# Revit family: assa_abloy_sw200i_13
name_source: partatom
category: Doors
units: mm (PartAtom-declared; Revit-internal decimal feet)

## family parameters
Always vertical = Yes
Classification Number = 23.30.10.00
Cut with Voids When Loaded = No
Host = Wall
Room Calculation Point = No
Shared = No

## types (1)
- assa_abloy_sw200i_13
    Analytic Construction = <None>
    BIMobject category = Swing Doors
    Bottom Profile Height = Leaf : 0' 4''
    Bottom Profile Option 01 = Leaf : 0' 4''
    Bottom Profile Option 02 = Leaf : 0' 7''
    Bottom Profile Option 03 = Leaf : 0' 10''
    Bottom Profile Option 04 = Leaf : 0' 12''
    Brass Polished Finish = Brass, Polished
    Brass Satin Finish = Brass, Satin
    Clear Anodized = Clear Anodized
    Dark Bronze Anodized = Dark Bronze Anodized
    Date of publishing = 2015-02-23
    Depth = 0.00
    Dimensions Overconstraint = No
    Edition number = 1
    Frame Material = Clear Anodized
    Function = Interior
    Gap = 0' - 0 1/4"
    Glass = Glass
    Height = 6' - 11 3/4"
    IFC Classification = Door
    Manufacturer name = Besam-North America
    Material main = Aluminium
    Nominal height = 0.00
    Nominal width = 0.00
    Product SKU = SW200i_OHC
    Product data url = http://besam-na.bimobject.com
    Product family = Swing
    Product group = Overhead Concealed
    QR code = http://besam-na.bimobject.com
    Rough Height = 7' - 0"
    Rough Width = 3' - 5"
    Stainless Steel Polished Finish = Stainless Steel, Polished
    Stainless Steel Satin Finish = Stainless Steel, Satin
    Thickness = 3' - 0"
    UNSPSC Code = 30171511
    Uniclass 1.4 Code = L81323
    Uniclass 1.4 Description = Swings
    Wall Closure = By host
    Weight Net (Kg) = 0
    Width = 3' - 4 1/2"

## geometry (parser evidence)
native form markers: Blend x2, Sweep x26
no freeform markers — native parametric forms only
